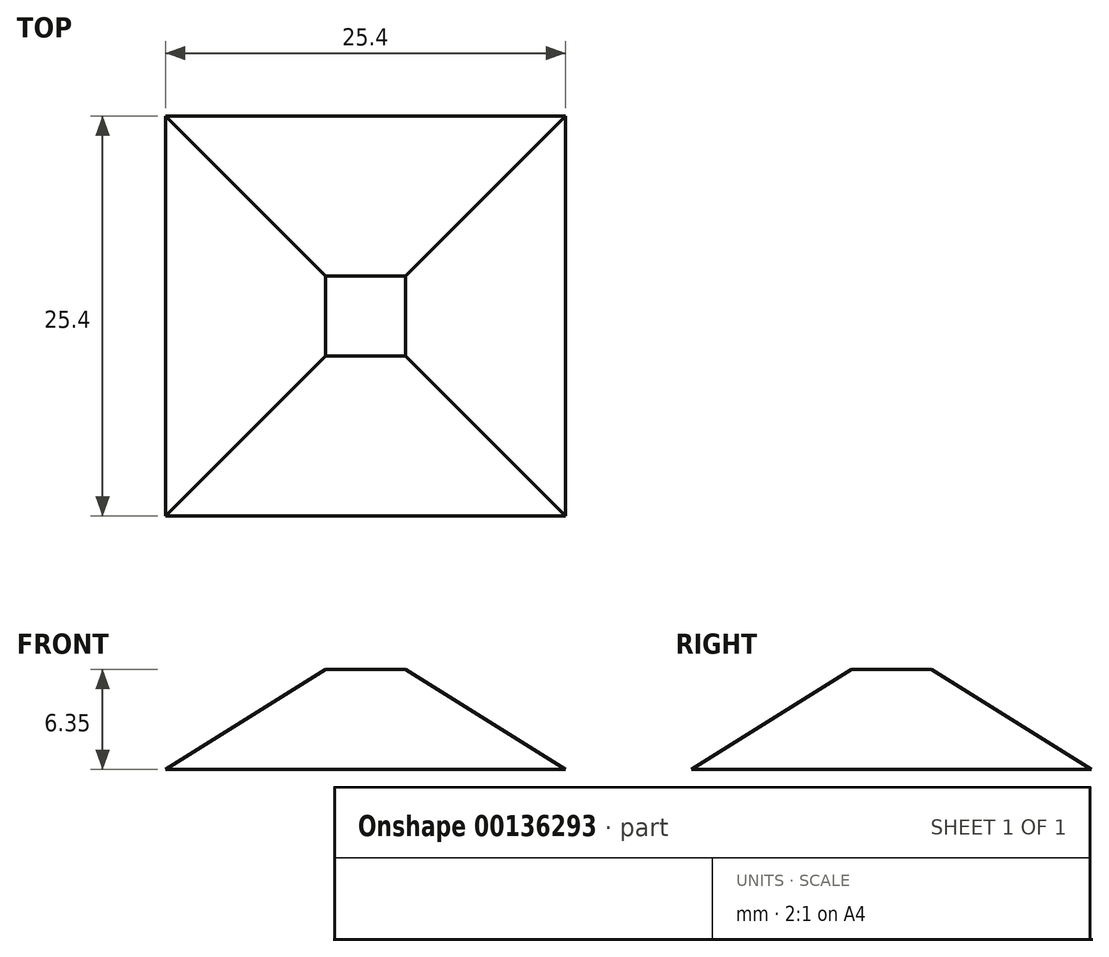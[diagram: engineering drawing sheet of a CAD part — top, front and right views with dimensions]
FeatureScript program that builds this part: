
annotation { "Feature Type Name" : "Feature", "Feature Type Description" : "" }
export const myFeature = defineFeature(function(context is Context, id is Id, definition is map)
    precondition{}
    {
        {
            var Q0;
            Q0=qCreatedBy(makeId("Top.planeOp"),FACE);
            var sketch = newSketch(context, id + "F0", { "sketchPlane" : qUnion([Q0])});
            skLineSegment(sketch, "E0.bottom", {"start": v(-19.24, 16.4) * mm, "end": v(6.16, 16.4) * mm});
            skLineSegment(sketch, "E0.top", {"start": v(-19.24, -9) * mm, "end": v(6.16, -9) * mm});
            skLineSegment(sketch, "E0.left", {"start": v(-19.24, 16.4) * mm, "end": v(-19.24, -9) * mm});
            skLineSegment(sketch, "E0.right", {"start": v(6.16, 16.4) * mm, "end": v(6.16, -9) * mm});
            skSolve(sketch);
        }
        {
            var Q0;
            Q0=makeQuery(id+"F0.imprint","IMPRINT",FACE,{"disambiguationData":[TD([[makeQuery(id+"F0.imprint","IMPRINT",EDGE,{"derivedFrom":sQuery(id+"F0.wireOp",EDGE,"E0.bottom")}),-1.0]])]});
            extrude(context, id + "F1", {"entities" : qUnion([Q0]), "depth" : 6.35 * mm});
        }
        {
            var Q0;
            Q0=makeQuery(id+"F1.opExtrude","CAP_FACE",FACE,{"disambiguationData":[OSD([sQuery(id+"F0.wireOp",EDGE,"E0.bottom"),sQuery(id+"F0.wireOp",EDGE,"E0.top"),sQuery(id+"F0.wireOp",EDGE,"E0.left"),sQuery(id+"F0.wireOp",EDGE,"E0.right")])],"isStart":false});
            chamfer(context, id + "F2", {"entities" : qUnion([Q0]), "chamferType" : ChamferType.TWO_OFFSETS, "width1" : 6.35 * mm, "oppositeDirection" : false, "width2" : 10.16 * mm, "tangentPropagation" : true});
        }
    });
